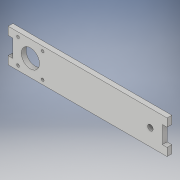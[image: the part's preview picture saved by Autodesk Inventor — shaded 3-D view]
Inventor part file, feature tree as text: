
AUTODESK INVENTOR PART (.ipt)
format: ipt  version: 2019 (Build 230136000, 136)  size: 133,632 bytes
history: native  units: mm
features: extrude x1, sketch x1
ambient origin geometry x8: Origin, YZ Plane, XZ Plane, XY Plane, X Axis, Y Axis, Z Axis, Center Point
bodies: Body1 (feature_tree)
feature tree (2):
  extrude  "Extrusion2"  Depth=3.5mm
  sketch  "Sketch1"  dims[d13=3.5mm d14=3.5mm d15=15.5mm d16=15.5mm d21=3.5mm d22=3.5mm d23=31.0mm d24=23.0mm d25=6.0mm d26=0.0mm d29=21.0mm d30=15.5mm d31=200.0mm d32=21.0mm d34=21.0mm d35=6.0mm d36=10.0mm d37=10.0mm d38=28.0mm d39=10.0mm d40=10.0mm d41=6.0mm d42=7.0mm d43=15.0mm d44=21.0mm]
